# Revit family: FEN2_63_UN_Surface-mounted_ETK
name_source: partatom
category: Lighting Fixtures
revit_build: Autodesk Revit 2017 (Build: 20190508_0315(x64)
units: mm (PartAtom-declared; Revit-internal decimal feet)

## family parameters
Always vertical = Yes
Cut with Voids When Loaded = No
Light Source = No
OmniClass Number = 23.80.70.11.14.11
OmniClass Title = Downlights
Part Type = Normal
Room Calculation Point = Yes
Round Connector Dimension = Use Diameter
Shared = No
Work Plane-Based = No

## types (8) — shared parameters
Apparent Load = 23 VA
Assembly Code = 63.0
Description = Surface Mounted
IfcExportAs = IfcLightFixtureType
IfcExportType = USERDEFINED
Lamp = LED
Light Source = FEN.2 - Lightsource : FEN.2101.xx - 23W / 700-1960lm / 3000K
Luminaire_Body_Material = 11 Matt white
Manufacturer = ETK licht B.V.
Model = FEN2
Type Comments = IP66 - IK10
URL = https://www.etk.nl
Voltage = 230 V
Wattage Comments = 23W

## type names (no varying parameters)
- FEN.2101.xx  -23W / 700-1960lm / 3000K
- FEN.2201.xx  -23W / 720-2930lm / 4000K
- FEN.2103.xx  -23W / 700-1960lm / 3000K
- FEN.2111.xx  -23W / 700-1960lm / 3000K
- FEN.2121.xx  -23W / 700-1960lm / 3000K
- FEN.2203.xx  -23W / 720-2930lm / 4000K
- FEN.2211.xx  -23W / 720-2930lm / 4000K
- FEN.2221.xx  -23W / 720-2930lm / 4000K

## geometry (parser evidence)
native form markers: Sweep x10
no freeform markers — native parametric forms only
